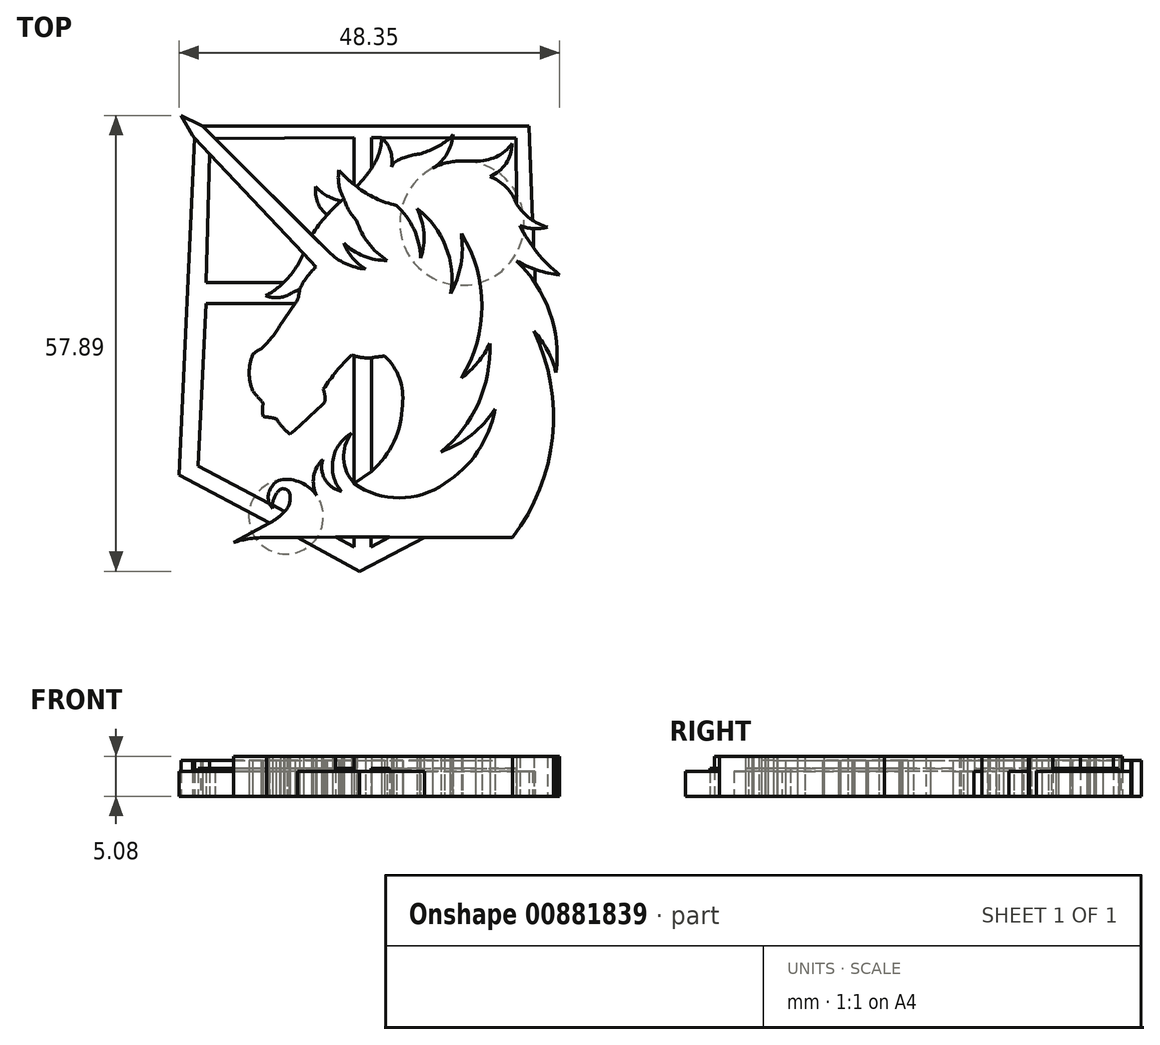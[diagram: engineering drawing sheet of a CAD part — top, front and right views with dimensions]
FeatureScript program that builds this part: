
annotation { "Feature Type Name" : "Feature", "Feature Type Description" : "" }
export const myFeature = defineFeature(function(context is Context, id is Id, definition is map)
    precondition{}
    {
        {
            var Q0;
            Q0=qCreatedBy(makeId("Top.planeOp"),FACE);
            var sketch = newSketch(context, id + "F0", { "sketchPlane" : qUnion([Q0])});
            skLineSegment(sketch, "E0", {"start": v(-21.03, 23.94) * mm, "end": v(-23.04, -18.87) * mm});
            skLineSegment(sketch, "E1", {"start": v(-23.04, -18.87) * mm, "end": v(-11.54, -25) * mm});
            skLineSegment(sketch, "E2", {"start": v(-7.98, -26.8) * mm, "end": v(-0.07, -31.13) * mm});
            skLineSegment(sketch, "E3", {"start": v(-0.07, -31.13) * mm, "end": v(8.15, -26.82) * mm});
            skLineSegment(sketch, "E4", {"start": v(21.9, 13.46) * mm, "end": v(21.4, 25.42) * mm});
            skLineSegment(sketch, "E5", {"start": v(21.4, 25.42) * mm, "end": v(-20.04, 25.42) * mm});
            skLineSegment(sketch, "E6", {"start": v(-0.78, 18) * mm, "end": v(-0.78, 24) * mm});
            skLineSegment(sketch, "E7", {"start": v(-0.78, 24) * mm, "end": v(-18.46, 23.84) * mm});
            skLineSegment(sketch, "E8", {"start": v(1.4, 20.05) * mm, "end": v(1.4, 23.99) * mm});
            skLineSegment(sketch, "E9", {"start": v(1.4, 23.99) * mm, "end": v(11.41, 23.91) * mm});
            skLineSegment(sketch, "E10", {"start": v(11.71, 23.88) * mm, "end": v(19.75, 23.88) * mm});
            skLineSegment(sketch, "E11", {"start": v(19.75, 23.88) * mm, "end": v(19.87, 15.55) * mm});
            skLineSegment(sketch, "E12", {"start": v(-19.15, 21.9) * mm, "end": v(-19.56, 5.54) * mm});
            skLineSegment(sketch, "E13", {"start": v(-19.56, 5.54) * mm, "end": v(-9.77, 5.54) * mm});
            skLineSegment(sketch, "E14", {"start": v(-8.28, 2.86) * mm, "end": v(-19.6, 2.86) * mm});
            skLineSegment(sketch, "E15", {"start": v(-19.6, 2.86) * mm, "end": v(-20.63, -17.77) * mm});
            skLineSegment(sketch, "E16", {"start": v(-20.63, -17.77) * mm, "end": v(-11.57, -22.5) * mm});
            skLineSegment(sketch, "E17", {"start": v(-11.16, -22.7) * mm, "end": v(-9.61, -23.51) * mm});
            skLineSegment(sketch, "E18", {"start": v(-3.18, -26.77) * mm, "end": v(-0.78, -28.04) * mm});
            skLineSegment(sketch, "E19", {"start": v(-0.78, -28.04) * mm, "end": v(-0.78, -26.78) * mm});
            skLineSegment(sketch, "E20", {"start": v(1.37, -26.78) * mm, "end": v(1.37, -28.04) * mm});
            skLineSegment(sketch, "E21", {"start": v(1.37, -28.04) * mm, "end": v(3.74, -26.78) * mm});
            skLineSegment(sketch, "E22", {"start": v(-7.98, -26.8) * mm, "end": v(-3.18, -26.77) * mm});
            skLineSegment(sketch, "E23", {"start": v(-0.78, -26.78) * mm, "end": v(-3.18, -26.77) * mm});
            skLineSegment(sketch, "E24", {"start": v(1.37, -26.78) * mm, "end": v(-0.78, -26.78) * mm});
            skLineSegment(sketch, "E25", {"start": v(1.37, -26.78) * mm, "end": v(3.74, -26.78) * mm});
            skLineSegment(sketch, "E26", {"start": v(3.74, -26.78) * mm, "end": v(8.15, -26.82) * mm});
            skLineSegment(sketch, "E27", {"start": v(8.15, -26.82) * mm, "end": v(19.34, -26.82) * mm});
            skLineSegment(sketch, "E28", {"start": v(-0.77, -3.75) * mm, "end": v(-0.77, -19.96) * mm});
            skLineSegment(sketch, "E29", {"start": v(1.4, -18.43) * mm, "end": v(1.4, -4) * mm});
            skArc(sketch, "E30", {"start": v(19.34, -26.82) * mm, "mid": v(24.4, -14.1) * mm, "end": v(22.06, -0.62) * mm});
            skArc(sketch, "E31", {"start": v(24.85, -5.85) * mm, "mid": v(23.78, -3.06) * mm, "end": v(22.06, -0.62) * mm});
            skArc(sketch, "E32", {"start": v(24.85, -5.85) * mm, "mid": v(24.04, 1.83) * mm, "end": v(19.84, 8.3) * mm});
            skArc(sketch, "E33", {"start": v(19.84, 8.3) * mm, "mid": v(22.48, 7.12) * mm, "end": v(25.3, 6.54) * mm});
            skLineSegment(sketch, "E34", {"start": v(22.2, 7.21) * mm, "end": v(22.2, 5.5) * mm});
            skArc(sketch, "E35", {"start": v(20.27, 12.78) * mm, "mid": v(22.46, 9.39) * mm, "end": v(25.3, 6.54) * mm});
            skArc(sketch, "E36", {"start": v(20.27, 12.78) * mm, "mid": v(22.01, 12.4) * mm, "end": v(23.79, 12.58) * mm});
            skArc(sketch, "E37", {"start": v(19.87, 15.55) * mm, "mid": v(21.55, 13.7) * mm, "end": v(23.79, 12.58) * mm});
            skLineSegment(sketch, "E38", {"start": v(22.01, 12.4) * mm, "end": v(22.01, 9.96) * mm});
            skLineSegment(sketch, "E39", {"start": v(-5.62, 7.54) * mm, "end": v(-19.15, 21.9) * mm});
            skLineSegment(sketch, "E40", {"start": v(-19.15, 21.9) * mm, "end": v(-21.03, 23.94) * mm});
            skLineSegment(sketch, "E41", {"start": v(-21.03, 23.94) * mm, "end": v(-21.3, 24.2) * mm});
            skLineSegment(sketch, "E42", {"start": v(-21.3, 24.2) * mm, "end": v(-22.76, 26.76) * mm});
            skLineSegment(sketch, "E43", {"start": v(-22.76, 26.76) * mm, "end": v(-20.26, 25.56) * mm});
            skLineSegment(sketch, "E44", {"start": v(-20.26, 25.56) * mm, "end": v(-20.04, 25.42) * mm});
            skLineSegment(sketch, "E45", {"start": v(-20.04, 25.42) * mm, "end": v(-18.46, 23.84) * mm});
            skLineSegment(sketch, "E46", {"start": v(-18.46, 23.84) * mm, "end": v(-4.05, 9.47) * mm});
            skLineSegment(sketch, "E47", {"start": v(-5.62, 7.54) * mm, "end": v(-4.05, 9.47) * mm});
            skArc(sketch, "E48", {"start": v(-8.28, 2.86) * mm, "mid": v(-7.88, 3.72) * mm, "end": v(-7.73, 4.67) * mm});
            skArc(sketch, "E49", {"start": v(-12.04, 3.88) * mm, "mid": v(-10.84, 4.61) * mm, "end": v(-9.77, 5.54) * mm});
            skArc(sketch, "E50", {"start": v(-12.04, 3.88) * mm, "mid": v(-10.69, 3.64) * mm, "end": v(-9.33, 3.88) * mm});
            skArc(sketch, "E51", {"start": v(-7.73, 4.67) * mm, "mid": v(-8.55, 4.31) * mm, "end": v(-9.33, 3.88) * mm});
            skLineSegment(sketch, "E52", {"start": v(-16.12, -27.46) * mm, "end": v(-11.54, -25) * mm});
            skArc(sketch, "E53", {"start": v(-11.54, -25) * mm, "mid": v(-10.51, -24.34) * mm, "end": v(-9.61, -23.51) * mm});
            skArc(sketch, "E54", {"start": v(-11.9, -26.84) * mm, "mid": v(-14.03, -26.98) * mm, "end": v(-16.12, -27.46) * mm});
            skLineSegment(sketch, "E55", {"start": v(-11.9, -26.84) * mm, "end": v(-7.98, -26.8) * mm});
            skArc(sketch, "E56", {"start": v(-9.61, -23.51) * mm, "mid": v(-8.97, -22.37) * mm, "end": v(-9.04, -21.07) * mm});
            skArc(sketch, "E57", {"start": v(-10.12, -20.67) * mm, "mid": v(-10.84, -21.59) * mm, "end": v(-11.16, -22.7) * mm});
            skArc(sketch, "E58", {"start": v(-9.04, -21.07) * mm, "mid": v(-9.52, -20.7) * mm, "end": v(-10.12, -20.67) * mm});
            skLineSegment(sketch, "E59", {"start": v(-11.16, -22.7) * mm, "end": v(-11.16, -23.14) * mm});
            skLineSegment(sketch, "E60", {"start": v(-11.16, -23.14) * mm, "end": v(-11.57, -22.5) * mm});
            skArc(sketch, "E61", {"start": v(-10.15, -19.5) * mm, "mid": v(-11.47, -20.71) * mm, "end": v(-11.57, -22.5) * mm});
            skArc(sketch, "E62", {"start": v(-5.53, -21.51) * mm, "mid": v(-7.55, -19.85) * mm, "end": v(-10.15, -19.5) * mm});
            skArc(sketch, "E63", {"start": v(-4.75, -16.9) * mm, "mid": v(-5.92, -19.08) * mm, "end": v(-5.53, -21.51) * mm});
            skArc(sketch, "E64", {"start": v(-4.75, -16.9) * mm, "mid": v(-4.49, -19.47) * mm, "end": v(-2.4, -20.97) * mm});
            skArc(sketch, "E65", {"start": v(-1.1, -13.57) * mm, "mid": v(-3.48, -16.96) * mm, "end": v(-2.4, -20.97) * mm});
            skArc(sketch, "E66", {"start": v(-1.1, -13.57) * mm, "mid": v(-2.13, -16.83) * mm, "end": v(-0.77, -19.96) * mm});
            skLineSegment(sketch, "E67", {"start": v(-0.77, -19.96) * mm, "end": v(1.4, -18.43) * mm});
            skArc(sketch, "E68", {"start": v(-0.77, -3.75) * mm, "mid": v(0.3, -3.99) * mm, "end": v(1.4, -4) * mm});
            skArc(sketch, "E69", {"start": v(-0.77, -19.96) * mm, "mid": v(4.96, -21.8) * mm, "end": v(10.69, -19.96) * mm});
            skArc(sketch, "E70", {"start": v(10.69, -19.96) * mm, "mid": v(14.92, -15.92) * mm, "end": v(17.1, -10.5) * mm});
            skArc(sketch, "E71", {"start": v(10.26, -15.95) * mm, "mid": v(14.13, -13.79) * mm, "end": v(17.1, -10.5) * mm});
            skArc(sketch, "E72", {"start": v(10.26, -15.95) * mm, "mid": v(14.99, -9.8) * mm, "end": v(16.45, -2.17) * mm});
            skArc(sketch, "E73", {"start": v(12.83, -6.57) * mm, "mid": v(14.92, -4.6) * mm, "end": v(16.45, -2.17) * mm});
            skArc(sketch, "E74", {"start": v(12.83, -6.57) * mm, "mid": v(15.46, 2.6) * mm, "end": v(12.83, 11.76) * mm});
            skArc(sketch, "E75", {"start": v(11.48, 4.15) * mm, "mid": v(12.77, 7.85) * mm, "end": v(12.83, 11.76) * mm});
            skArc(sketch, "E76", {"start": v(11.48, 4.15) * mm, "mid": v(10.85, 10.15) * mm, "end": v(7.22, 14.97) * mm});
            skArc(sketch, "E77", {"start": v(7.67, 8.66) * mm, "mid": v(8.07, 11.86) * mm, "end": v(7.22, 14.97) * mm});
            skArc(sketch, "E78", {"start": v(7.67, 8.66) * mm, "mid": v(6.8, 12.32) * mm, "end": v(4.57, 15.36) * mm});
            skArc(sketch, "E79", {"start": v(-0.78, 18) * mm, "mid": v(1.73, 16.35) * mm, "end": v(4.57, 15.36) * mm});
            skArc(sketch, "E80", {"start": v(-2.73, 19.86) * mm, "mid": v(-1.8, 18.88) * mm, "end": v(-0.78, 18) * mm});
            skArc(sketch, "E81", {"start": v(-2.73, 19.86) * mm, "mid": v(-2.71, 17.98) * mm, "end": v(-2.1, 16.22) * mm});
            skArc(sketch, "E82", {"start": v(-2.1, 16.22) * mm, "mid": v(-4.3, 14.05) * mm, "end": v(-6.17, 11.58) * mm});
            skArc(sketch, "E83", {"start": v(-4.05, 9.47) * mm, "mid": v(-1.87, 7.95) * mm, "end": v(0.7, 7.27) * mm});
            skArc(sketch, "E84", {"start": v(-2.1, 10.57) * mm, "mid": v(-0.98, 8.69) * mm, "end": v(0.7, 7.27) * mm});
            skArc(sketch, "E85", {"start": v(-2.1, 10.57) * mm, "mid": v(0.44, 8.9) * mm, "end": v(3.42, 8.37) * mm});
            skArc(sketch, "E86", {"start": v(-0.47, 13.42) * mm, "mid": v(1.02, 10.54) * mm, "end": v(3.42, 8.37) * mm});
            skArc(sketch, "E87", {"start": v(-2.1, 16.22) * mm, "mid": v(-1.45, 14.72) * mm, "end": v(-0.47, 13.42) * mm});
            skArc(sketch, "E88", {"start": v(-9.77, 5.54) * mm, "mid": v(-8.3, 7.25) * mm, "end": v(-7.24, 9.26) * mm});
            skArc(sketch, "E89", {"start": v(-5.62, 7.54) * mm, "mid": v(-6.81, 6.2) * mm, "end": v(-7.73, 4.67) * mm});
            skArc(sketch, "E90", {"start": v(19.87, 15.55) * mm, "mid": v(18.53, 17.66) * mm, "end": v(16.44, 19) * mm});
            skArc(sketch, "E91", {"start": v(16.44, 19) * mm, "mid": v(18.5, 20.69) * mm, "end": v(19.29, 23.22) * mm});
            skArc(sketch, "E92", {"start": v(14.6, 21) * mm, "mid": v(17.23, 21.52) * mm, "end": v(19.29, 23.22) * mm});
            skLineSegment(sketch, "E93", {"start": v(14.6, 21) * mm, "end": v(12.92, 21) * mm});
            skArc(sketch, "E94", {"start": v(12.92, 21) * mm, "mid": v(10.99, 20.77) * mm, "end": v(9.18, 20.07) * mm});
            skArc(sketch, "E95", {"start": v(9.18, 20.07) * mm, "mid": v(10.87, 21.69) * mm, "end": v(11.71, 23.88) * mm});
            skLineSegment(sketch, "E96", {"start": v(11.71, 23.88) * mm, "end": v(11.78, 24.34) * mm});
            skLineSegment(sketch, "E97", {"start": v(11.78, 24.34) * mm, "end": v(11.41, 23.91) * mm});
            skArc(sketch, "E98", {"start": v(7.51, 21.87) * mm, "mid": v(9.57, 22.69) * mm, "end": v(11.41, 23.91) * mm});
            skArc(sketch, "E99", {"start": v(7.51, 21.87) * mm, "mid": v(5.8, 21.51) * mm, "end": v(4.21, 20.76) * mm});
            skLineSegment(sketch, "E100", {"start": v(4.21, 20.76) * mm, "end": v(3.96, 20.25) * mm});
            skArc(sketch, "E101", {"start": v(3.96, 20.25) * mm, "mid": v(3.82, 22.27) * mm, "end": v(2.72, 23.98) * mm});
            skArc(sketch, "E102", {"start": v(1.4, 20.05) * mm, "mid": v(2.36, 21.91) * mm, "end": v(2.72, 23.98) * mm});
            skArc(sketch, "E103", {"start": v(-0.45, 17.73) * mm, "mid": v(0.52, 18.86) * mm, "end": v(1.4, 20.05) * mm});
            skArc(sketch, "E104", {"start": v(1.4, -18.43) * mm, "mid": v(4.3, -14.64) * mm, "end": v(5.34, -10) * mm});
            skArc(sketch, "E105", {"start": v(5.34, -10) * mm, "mid": v(4.98, -6.62) * mm, "end": v(3.1, -3.8) * mm});
            skArc(sketch, "E106", {"start": v(3.1, -3.8) * mm, "mid": v(2.24, -3.88) * mm, "end": v(1.4, -4) * mm});
            skLineSegment(sketch, "E107", {"start": v(-0.77, -3.75) * mm, "end": v(-1.13, -3.63) * mm});
            skArc(sketch, "E108", {"start": v(-1.13, -3.63) * mm, "mid": v(-3.02, -5.72) * mm, "end": v(-4.7, -7.98) * mm});
            skArc(sketch, "E109", {"start": v(-4.53, -9.7) * mm, "mid": v(-4.5, -8.83) * mm, "end": v(-4.7, -7.98) * mm});
            skArc(sketch, "E110", {"start": v(-8.9, -13.71) * mm, "mid": v(-6.7, -11.7) * mm, "end": v(-4.53, -9.7) * mm});
            skArc(sketch, "E111", {"start": v(-10.69, -11.73) * mm, "mid": v(-9.9, -12.81) * mm, "end": v(-8.9, -13.71) * mm});
            skArc(sketch, "E112", {"start": v(-10.69, -11.73) * mm, "mid": v(-11.51, -11.58) * mm, "end": v(-12.34, -11.47) * mm});
            skArc(sketch, "E113", {"start": v(-12.34, -9.78) * mm, "mid": v(-12.42, -10.63) * mm, "end": v(-12.34, -11.47) * mm});
            skArc(sketch, "E114", {"start": v(-13.66, -8.21) * mm, "mid": v(-13.01, -9) * mm, "end": v(-12.34, -9.78) * mm});
            skArc(sketch, "E115", {"start": v(-13.66, -3.6) * mm, "mid": v(-14.12, -5.9) * mm, "end": v(-13.66, -8.21) * mm});
            skArc(sketch, "E116", {"start": v(-12.61, -2.88) * mm, "mid": v(-13.17, -3.19) * mm, "end": v(-13.66, -3.6) * mm});
            skArc(sketch, "E117", {"start": v(-12.61, -2.88) * mm, "mid": v(-11.34, -1.53) * mm, "end": v(-10.27, 0) * mm});
            skLineSegment(sketch, "E118", {"start": v(-10.27, 0) * mm, "end": v(-8.28, 2.86) * mm});
            skArc(sketch, "E119", {"start": v(-5.66, 17.72) * mm, "mid": v(-5.43, 15.73) * mm, "end": v(-4.22, 14.14) * mm});
            skArc(sketch, "E120", {"start": v(-5.66, 17.72) * mm, "mid": v(-4.2, 16.56) * mm, "end": v(-2.45, 15.9) * mm});
            skSolve(sketch);
        }
        {
            var Q0;
            {var subQ5=sQuery(id+"F0.wireOp",EDGE,"E4");Q0=makeQuery(id+"F0.imprint","IMPRINT",FACE,{"disambiguationData":[TD([[makeQuery(id+"F0.imprint","IMPRINT",EDGE,{"derivedFrom":subQ5}),1.0]])]});}
            var Q1;
            Q1=makeQuery(id+"F0.imprint","IMPRINT",FACE,{"disambiguationData":[TD([[makeQuery(id+"F0.imprint","IMPRINT",EDGE,{"derivedFrom":sQuery(id+"F0.wireOp",EDGE,"E0")}),1.0]])]});
            var Q2;
            {var subQ3=sQuery(id+"F0.wireOp",EDGE,"E38");Q2=makeQuery(id+"F0.imprint","IMPRINT",FACE,{"disambiguationData":[TD([[makeQuery(id+"F0.imprint","IMPRINT",EDGE,{"derivedFrom":subQ3}),-1.0]])]});}
            var Q3;
            {var subQ3=sQuery(id+"F0.wireOp",EDGE,"E34");Q3=makeQuery(id+"F0.imprint","IMPRINT",FACE,{"disambiguationData":[TD([[makeQuery(id+"F0.imprint","IMPRINT",EDGE,{"derivedFrom":subQ3}),-1.0]])]});}
            var Q4;
            Q4=makeQuery(id+"F0.imprint","IMPRINT",FACE,{"disambiguationData":[TD([[makeQuery(id+"F0.imprint","IMPRINT",EDGE,{"derivedFrom":sQuery(id+"F0.wireOp",EDGE,"E28")}),1.0]])]});
            var Q5;
            Q5=makeQuery(id+"F0.imprint","IMPRINT",FACE,{"disambiguationData":[TD([[makeQuery(id+"F0.imprint","IMPRINT",EDGE,{"derivedFrom":sQuery(id+"F0.wireOp",EDGE,"E2")}),1.0]])]});
            extrude(context, id + "F1", {"entities" : qUnion([Q0, Q1, Q2, Q3, Q4, Q5]), "depth" : 3.17 * mm, "offsetDistance" : 25.4 * mm});
        }
        {
            var Q0;
            Q0=makeQuery(id+"F0.imprint","IMPRINT",FACE,{"disambiguationData":[TD([[makeQuery(id+"F0.imprint","IMPRINT",EDGE,{"derivedFrom":sQuery(id+"F0.wireOp",EDGE,"E6")}),1.0]])]});
            var Q1;
            {var subQ0=sQuery(id+"F0.wireOp",EDGE,"E12");Q1=makeQuery(id+"F0.imprint","IMPRINT",FACE,{"disambiguationData":[TD([[makeQuery(id+"F0.imprint","IMPRINT",EDGE,{"derivedFrom":subQ0}),1.0]])]});}
            var Q2;
            Q2=makeQuery(id+"F0.imprint","IMPRINT",FACE,{"disambiguationData":[TD([[makeQuery(id+"F0.imprint","IMPRINT",EDGE,{"derivedFrom":sQuery(id+"F0.wireOp",EDGE,"E14")}),1.0]])]});
            var Q3;
            Q3=makeQuery(id+"F0.imprint","IMPRINT",FACE,{"disambiguationData":[TD([[makeQuery(id+"F0.imprint","IMPRINT",EDGE,{"derivedFrom":sQuery(id+"F0.wireOp",EDGE,"E29")}),-1.0]])]});
            var Q4;
            Q4=makeQuery(id+"F0.imprint","IMPRINT",FACE,{"disambiguationData":[TD([[makeQuery(id+"F0.imprint","IMPRINT",EDGE,{"derivedFrom":sQuery(id+"F0.wireOp",EDGE,"E10")}),-1.0]])]});
            var Q5;
            {var subQ0=sQuery(id+"F0.wireOp",EDGE,"E98");Q5=makeQuery(id+"F0.imprint","IMPRINT",FACE,{"disambiguationData":[TD([[makeQuery(id+"F0.imprint","IMPRINT",EDGE,{"derivedFrom":subQ0}),1.0]])]});}
            var Q6;
            {var subQ0=sQuery(id+"F0.wireOp",EDGE,"E8");Q6=makeQuery(id+"F0.imprint","IMPRINT",FACE,{"disambiguationData":[TD([[makeQuery(id+"F0.imprint","IMPRINT",EDGE,{"derivedFrom":subQ0}),-1.0]])]});}
            var Q7;
            Q7=makeQuery(id+"F0.imprint","IMPRINT",FACE,{"disambiguationData":[TD([[makeQuery(id+"F0.imprint","IMPRINT",EDGE,{"derivedFrom":sQuery(id+"F0.wireOp",EDGE,"E17")}),1.0]])]});
            var Q8;
            Q8=makeQuery(id+"F0.imprint","IMPRINT",FACE,{"disambiguationData":[TD([[makeQuery(id+"F0.imprint","IMPRINT",EDGE,{"derivedFrom":sQuery(id+"F0.wireOp",EDGE,"E18")}),1.0]])]});
            var Q9;
            Q9=makeQuery(id+"F0.imprint","IMPRINT",FACE,{"disambiguationData":[TD([[makeQuery(id+"F0.imprint","IMPRINT",EDGE,{"derivedFrom":sQuery(id+"F0.wireOp",EDGE,"E20")}),1.0]])]});
            extrude(context, id + "F2", {"entities" : qUnion([Q0, Q1, Q2, Q3, Q4, Q5, Q6, Q7, Q8, Q9]), "depth" : 3.56 * mm, "offsetDistance" : 25.4 * mm});
        }
        {
            var Q0;
            Q0=makeQuery(id+"F0.imprint","IMPRINT",FACE,{"disambiguationData":[TD([[makeQuery(id+"F0.imprint","IMPRINT",EDGE,{"derivedFrom":sQuery(id+"F0.wireOp",EDGE,"E49")}),-1.0]])]});
            var Q1;
            {var subQ6=sQuery(id+"F0.wireOp",EDGE,"E83");Q1=makeQuery(id+"F0.imprint","IMPRINT",FACE,{"disambiguationData":[TD([[makeQuery(id+"F0.imprint","IMPRINT",EDGE,{"derivedFrom":subQ6}),1.0]])]});}
            var Q2;
            Q2=makeQuery(id+"F0.imprint","IMPRINT",FACE,{"disambiguationData":[TD([[makeQuery(id+"F0.imprint","IMPRINT",EDGE,{"derivedFrom":sQuery(id+"F0.wireOp",EDGE,"E22")}),1.0]])]});
            extrude(context, id + "F3", {"entities" : qUnion([Q0, Q1, Q2]), "depth" : 5.08 * mm, "offsetDistance" : 25.4 * mm});
        }
        {
            var Q0;
            {var subQ6=sQuery(id+"F0.wireOp",EDGE,"E40");Q0=makeQuery(id+"F0.imprint","IMPRINT",FACE,{"disambiguationData":[TD([[makeQuery(id+"F0.imprint","IMPRINT",EDGE,{"derivedFrom":subQ6}),-1.0]])]});}
            var Q1;
            Q1=makeQuery(id+"F0.imprint","IMPRINT",FACE,{"disambiguationData":[TD([[makeQuery(id+"F0.imprint","IMPRINT",EDGE,{"derivedFrom":sQuery(id+"F0.wireOp",EDGE,"E47")}),-1.0]])]});
            var Q2;
            {var subQ0=sQuery(id+"F0.wireOp",EDGE,"E119");Q2=makeQuery(id+"F0.imprint","IMPRINT",FACE,{"disambiguationData":[TD([[makeQuery(id+"F0.imprint","IMPRINT",EDGE,{"derivedFrom":subQ0}),1.0]])]});}
            extrude(context, id + "F4", {"entities" : qUnion([Q0, Q1, Q2]), "depth" : 4.57 * mm, "offsetDistance" : 25.4 * mm});
        }
    });
